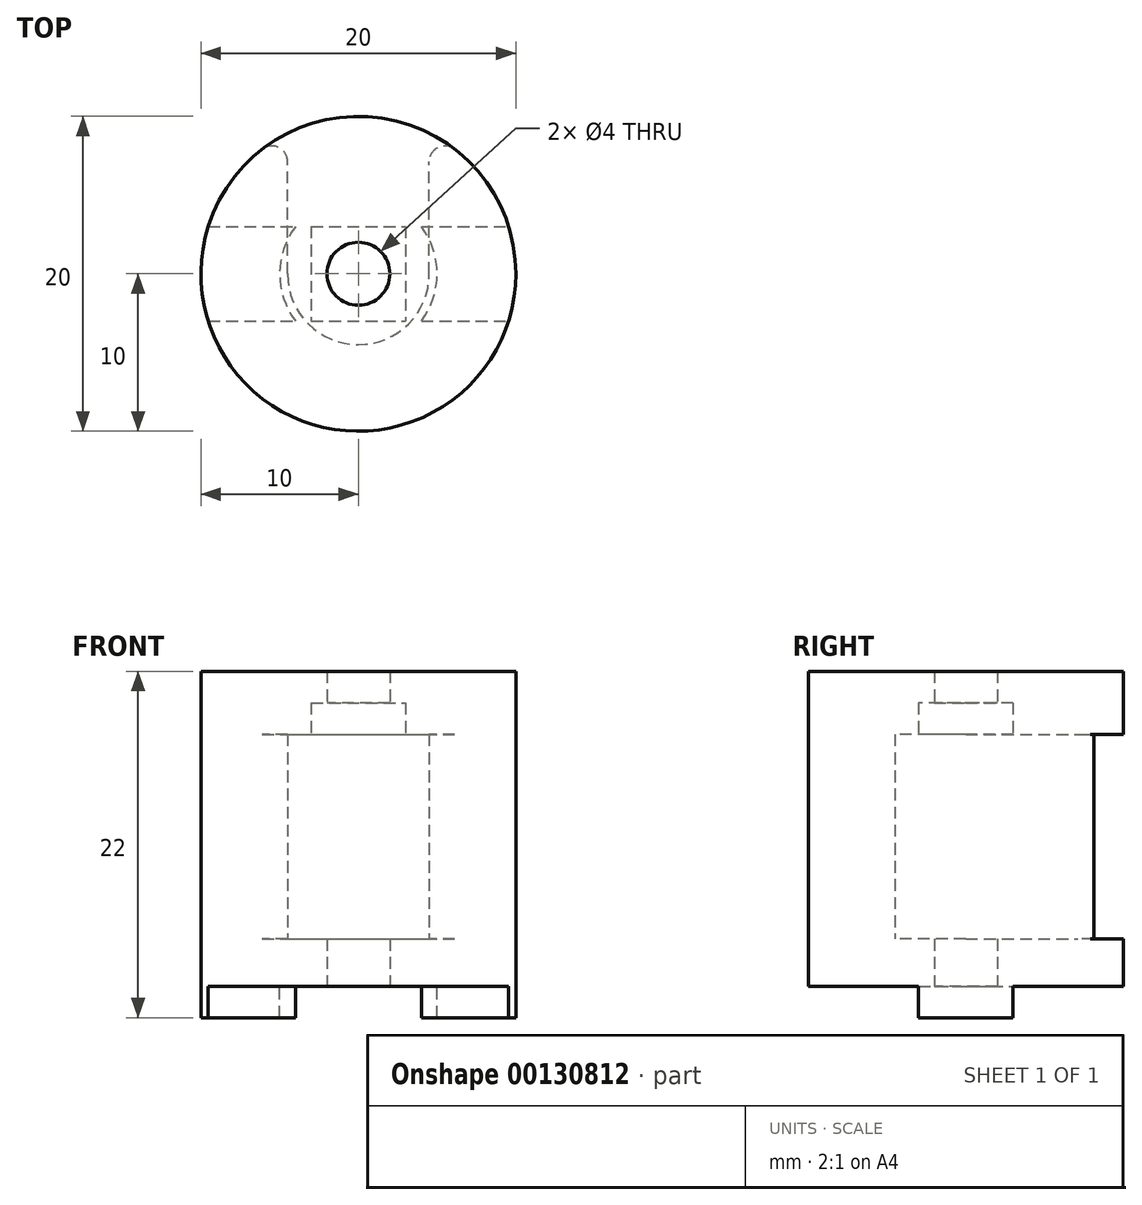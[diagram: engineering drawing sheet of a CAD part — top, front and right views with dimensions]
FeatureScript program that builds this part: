
annotation { "Feature Type Name" : "Feature", "Feature Type Description" : "" }
export const myFeature = defineFeature(function(context is Context, id is Id, definition is map)
    precondition{}
    {
        {
            var Q0;
            Q0=qCreatedBy(makeId("Top.planeOp"),FACE);
            var sketch = newSketch(context, id + "F0", { "sketchPlane" : qUnion([Q0])});
            skCircle(sketch, "E0", {"center": v(0, -10) * mm, "radius": 10 * mm});
            skSolve(sketch);
        }
        {
            var Q0;
            Q0=makeQuery(id+"F0.imprint","IMPRINT",FACE,{"disambiguationData":[TD([[makeQuery(id+"F0.imprint","IMPRINT",EDGE,{"derivedFrom":sQuery(id+"F0.wireOp",EDGE,"E0")}),1.0]])]});
            extrude(context, id + "F1", {"entities" : qUnion([Q0]), "depth" : 20 * mm});
        }
        {
            var Q0;
            Q0=makeQuery(id+"F1.opExtrude","CAP_FACE",FACE,{"disambiguationData":[OSD([sQuery(id+"F0.wireOp",EDGE,"E0")])],"isStart":true});
            var sketch = newSketch(context, id + "F2", { "sketchPlane" : qUnion([Q0])});
            skArc(sketch, "E1", {"start": v(9.54, 7) * mm, "mid": v(10, 10) * mm, "end": v(9.54, 13) * mm});
            skLineSegment(sketch, "E2", {"start": v(-9.54, 7) * mm, "end": v(-4, 7) * mm});
            skLineSegment(sketch, "E3", {"start": v(-9.54, 13) * mm, "end": v(-4, 13) * mm});
            skArc(sketch, "E4", {"start": v(-4, 13) * mm, "mid": v(-5, 10) * mm, "end": v(-4, 7) * mm});
            skLineSegment(sketch, "E5.trimOffspring", {"start": v(4, 13) * mm, "end": v(9.54, 13) * mm});
            skArc(sketch, "E6.trimOffspring", {"start": v(4, 7) * mm, "mid": v(5, 10) * mm, "end": v(4, 13) * mm});
            skLineSegment(sketch, "E7.trimOffspring", {"start": v(4, 7) * mm, "end": v(9.54, 7) * mm});
            skArc(sketch, "E8.trimOffspring", {"start": v(-9.54, 13) * mm, "mid": v(-10, 10) * mm, "end": v(-9.54, 7) * mm});
            skSolve(sketch);
        }
        {
            var Q0;
            Q0=makeQuery(id+"F2.imprint","IMPRINT",FACE,{"disambiguationData":[TD([[makeQuery(id+"F2.imprint","IMPRINT",EDGE,{"derivedFrom":sQuery(id+"F2.wireOp",EDGE,"E2")}),1.0]])]});
            var Q1;
            Q1=makeQuery(id+"F2.imprint","IMPRINT",FACE,{"disambiguationData":[TD([[makeQuery(id+"F2.imprint","IMPRINT",EDGE,{"derivedFrom":sQuery(id+"F2.wireOp",EDGE,"E1")}),-1.0]])]});
            extrude(context, id + "F3", {"entities" : qUnion([Q0, Q1]), "operationType" : NewBodyOperationType.ADD, "depth" : 2 * mm});
        }
        {
            var Q0;
            Q0=qCreatedBy(makeId("Top.planeOp"),FACE);
            cPlane(context, id + "F4", {"entities" : qUnion([Q0]), "cplaneType" : CPlaneType.OFFSET, "offset" : 3 * mm, "width" : 150 * mm, "height" : 150 * mm});
        }
        {
            var Q0;
            Q0=qCreatedBy(id+"F4.planeOp",FACE);
            var sketch = newSketch(context, id + "F5", { "sketchPlane" : qUnion([Q0])});
            skCircle(sketch, "E9", {"center": v(0, -10) * mm, "radius": 4.5 * mm});
            skSolve(sketch);
        }
        {
            var Q0;
            Q0=qSketchRegion(id+"F5",true);
            extrude(context, id + "F6", {"entities" : qUnion([Q0]), "operationType" : NewBodyOperationType.REMOVE, "depth" : 13 * mm});
        }
        {
            var Q0;
            Q0=makeQuery(id+"F1.opExtrude","CAP_FACE",FACE,{"disambiguationData":[OSD([sQuery(id+"F0.wireOp",EDGE,"E0")])],"isStart":true});
            var sketch = newSketch(context, id + "F7", { "sketchPlane" : qUnion([Q0])});
            skCircle(sketch, "E10", {"center": v(0, 10) * mm, "radius": 2 * mm});
            skSolve(sketch);
        }
        {
            var Q0;
            Q0=makeQuery(id+"F7.imprint","IMPRINT",FACE,{"disambiguationData":[TD([[makeQuery(id+"F7.imprint","IMPRINT",EDGE,{"derivedFrom":sQuery(id+"F7.wireOp",EDGE,"E10")}),1.0]])]});
            extrude(context, id + "F8", {"entities" : qUnion([Q0]), "operationType" : NewBodyOperationType.REMOVE, "endBound" : BoundingType.THROUGH_ALL, "oppositeDirection" : true, "depth" : 25 * mm});
        }
        {
            var Q0;
            Q0=qCreatedBy(makeId("Front.planeOp"),FACE);
            var sketch = newSketch(context, id + "F9", { "sketchPlane" : qUnion([Q0])});
            skLineSegment(sketch, "E11.bottom", {"start": v(4.5, 16) * mm, "end": v(-4.5, 16) * mm});
            skLineSegment(sketch, "E11.top", {"start": v(4.5, 3) * mm, "end": v(-4.5, 3) * mm});
            skLineSegment(sketch, "E11.left", {"start": v(4.5, 16) * mm, "end": v(4.5, 3) * mm});
            skLineSegment(sketch, "E11.right", {"start": v(-4.5, 16) * mm, "end": v(-4.5, 3) * mm});
            skSolve(sketch);
        }
        {
            var Q0;
            Q0=qSketchRegion(id+"F9",true);
            extrude(context, id + "F10", {"entities" : qUnion([Q0]), "operationType" : NewBodyOperationType.REMOVE, "depth" : 10 * mm});
        }
        {
            var Q0;
            Q0=makeQuery(id+"F10.boolean.opBoolean","MERGE",FACE,{"derivedFrom":[makeQuery(id+"F6.boolean.opBoolean","COPY",FACE,{"derivedFrom":makeQuery(id+"F6.opExtrude","CAP_FACE",FACE,{"disambiguationData":[OSD([sQuery(id+"F5.wireOp",EDGE,"E9")])],"isStart":false})}),makeQuery(id+"F10.opExtrude","SWEPT_FACE",FACE,{"disambiguationData":[OSD([sQuery(id+"F9.wireOp",EDGE,"E11.bottom")])]})]});
            var sketch = newSketch(context, id + "F11", { "sketchPlane" : qUnion([Q0])});
            skLineSegment(sketch, "E12.bottom", {"start": v(-3, 7) * mm, "end": v(3, 7) * mm});
            skLineSegment(sketch, "E12.top", {"start": v(-3, 13) * mm, "end": v(3, 13) * mm});
            skLineSegment(sketch, "E12.left", {"start": v(-3, 7) * mm, "end": v(-3, 13) * mm});
            skLineSegment(sketch, "E12.right", {"start": v(3, 7) * mm, "end": v(3, 13) * mm});
            skPoint(sketch, "E12.middle", {"position": v(0, 10) * mm});
            skSolve(sketch);
        }
        {
            var Q0;
            Q0=makeQuery(id+"F11.imprint","IMPRINT",FACE,{"disambiguationData":[TD([[makeQuery(id+"F11.imprint","IMPRINT",EDGE,{"derivedFrom":sQuery(id+"F11.wireOp",EDGE,"E12.bottom")}),1.0]])]});
            extrude(context, id + "F12", {"entities" : qUnion([Q0]), "operationType" : NewBodyOperationType.REMOVE, "oppositeDirection" : true, "depth" : 2 * mm});
        }
        {
            var Q0;
            Q0=makeQuery(id+"F10.boolean.opBoolean","INTERSECT",EDGE,{"derivedFrom":[makeQuery(id+"F3.boolean.opBoolean","MERGE",FACE,{"derivedFrom":[makeQuery(id+"F1.opExtrude","SWEPT_FACE",FACE,{"disambiguationData":[OSD([sQuery(id+"F0.wireOp",EDGE,"E0")])]}),makeQuery(id+"F3.opExtrude","SWEPT_FACE",FACE,{"disambiguationData":[OSD([sQuery(id+"F2.wireOp",EDGE,"E1")])]}),makeQuery(id+"F3.opExtrude","SWEPT_FACE",FACE,{"disambiguationData":[OSD([sQuery(id+"F2.wireOp",EDGE,"E8.trimOffspring")])]})]}),makeQuery(id+"F10.opExtrude","SWEPT_FACE",FACE,{"disambiguationData":[OSD([sQuery(id+"F9.wireOp",EDGE,"E11.left")])]})]});
            var Q1;
            Q1=makeQuery(id+"F10.boolean.opBoolean","INTERSECT",EDGE,{"derivedFrom":[makeQuery(id+"F3.boolean.opBoolean","MERGE",FACE,{"derivedFrom":[makeQuery(id+"F1.opExtrude","SWEPT_FACE",FACE,{"disambiguationData":[OSD([sQuery(id+"F0.wireOp",EDGE,"E0")])]}),makeQuery(id+"F3.opExtrude","SWEPT_FACE",FACE,{"disambiguationData":[OSD([sQuery(id+"F2.wireOp",EDGE,"E1")])]}),makeQuery(id+"F3.opExtrude","SWEPT_FACE",FACE,{"disambiguationData":[OSD([sQuery(id+"F2.wireOp",EDGE,"E8.trimOffspring")])]})]}),makeQuery(id+"F10.opExtrude","SWEPT_FACE",FACE,{"disambiguationData":[OSD([sQuery(id+"F9.wireOp",EDGE,"E11.right")])]})]});
            fillet(context, id + "F13", {"entities" : qUnion([Q0, Q1]), "radius" : 1 * mm, "tangentPropagation" : true, "allowEdgeOverflow" : false});
        }
    });
